# Revit family: 24-CH
name_source: partatom
category: Plumbing Fixtures
revit_build: Autodesk Revit 2015 (Build: 20140223_1515(x64)
units: mm (PartAtom-declared; Revit-internal decimal feet)

## types (1)
- 24-CH
    Body = Iron, Cast
    CW Connection = Yes
    Description = Coladera para Piso, una Boca con Rejilla Cuadrada
    Drain = Brass Chromed
    Garantía = El producto HELVEX está garantizado como libre de defectos en materiales y procesos de fabricación. El producto HELVEX está garantizado, en lo que se refiere a los acabados; por un periodo de 10 años en los acabados cromo y duravex, y por 2 años en cabados diferentes al cromo, a partir de la fecha de compra indicada en la factura.
    Grid = Stainless Steel
    Installation Thread = Diameter 2" NPSM (5.0 cm)
    Manufacturer = HELVEX S.A. DE C.V.
    Model = 24-CH
    Total Diameter = 7"
    Type Comments = Coladera para Piso
    Vent Connection = Yes

## geometry (parser evidence)
native form markers: Sweep x3
no freeform markers — native parametric forms only
